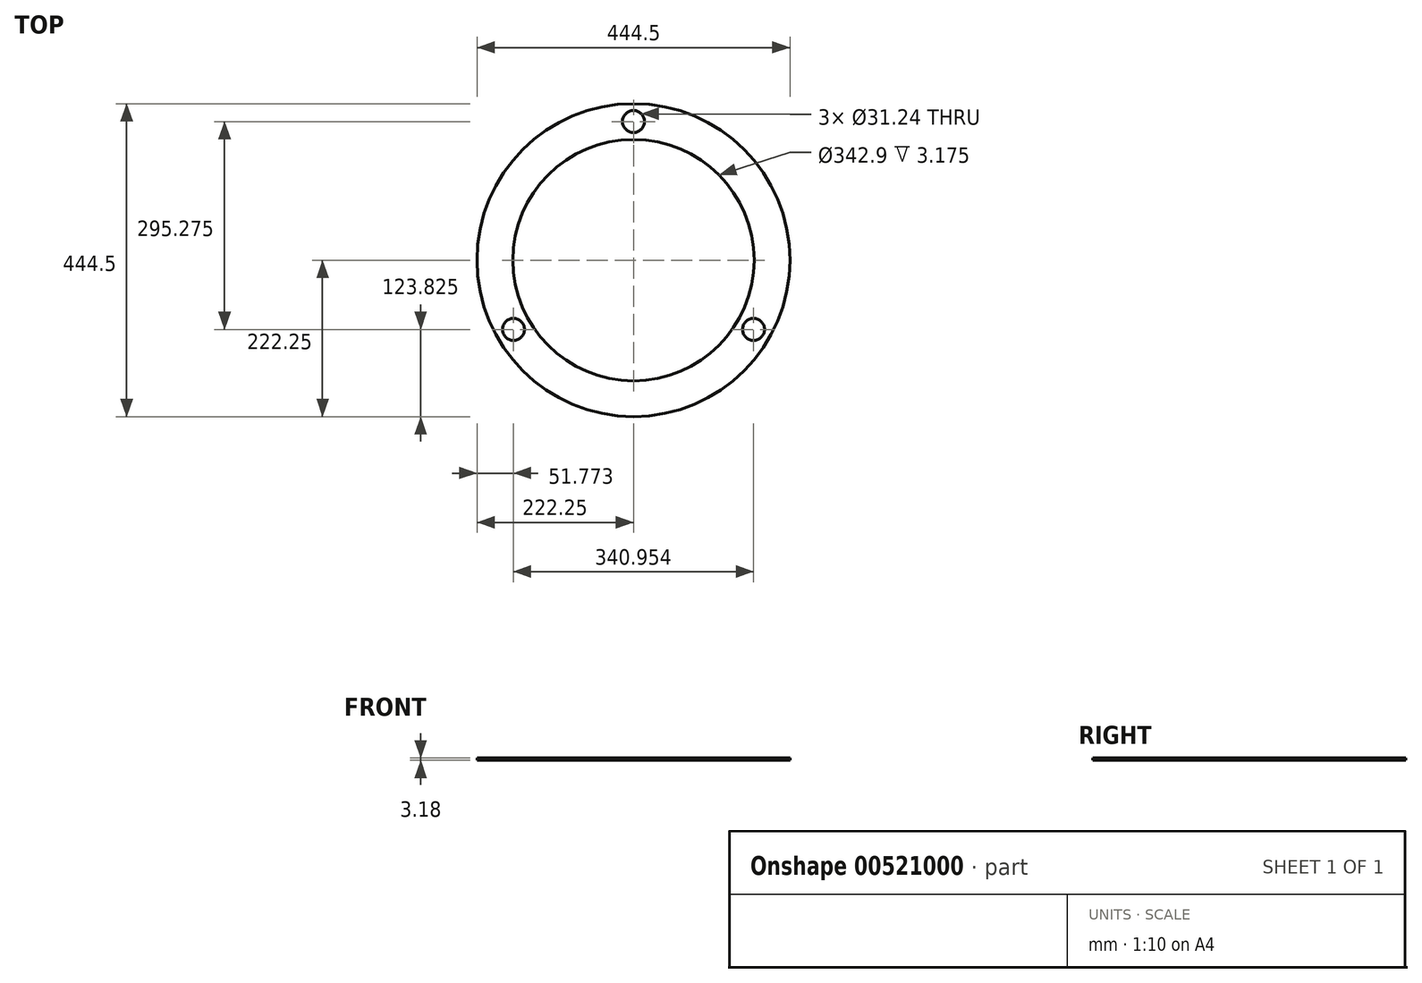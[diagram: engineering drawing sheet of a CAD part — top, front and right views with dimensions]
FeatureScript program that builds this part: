
annotation { "Feature Type Name" : "Feature", "Feature Type Description" : "" }
export const myFeature = defineFeature(function(context is Context, id is Id, definition is map)
    precondition{}
    {
        {
            var Q0;
            Q0=qCreatedBy(makeId("Top.planeOp"),FACE);
            var sketch = newSketch(context, id + "F0", { "sketchPlane" : qUnion([Q0])});
            skCircle(sketch, "E0", {"center": v(0, 0) * mm, "radius": 222.25 * mm});
            skCircle(sketch, "E1", {"center": v(0, 0) * mm, "radius": 171.45 * mm});
            skCircle(sketch, "E2", {"center": v(0, 196.85) * mm, "radius": 15.62 * mm});
            skCircle(sketch, "E3", {"center": v(170.48, -98.43) * mm, "radius": 15.62 * mm});
            skLineSegment(sketch, "E4", {"start": v(0, 259.12) * mm, "end": v(0, -278.93) * mm, "construction": true});
            skLineSegment(sketch, "E5", {"start": v(0, 0) * mm, "end": v(289.5, -167.14) * mm, "construction": true});
            skLineSegment(sketch, "E6", {"start": v(0, 0) * mm, "end": v(-307.83, -177.73) * mm, "construction": true});
            skCircle(sketch, "E7", {"center": v(-170.48, -98.43) * mm, "radius": 15.62 * mm});
            skSolve(sketch);
        }
        {
            var Q0;
            Q0=makeQuery(id+"F0.imprint","IMPRINT",FACE,{"disambiguationData":[TD([[makeQuery(id+"F0.imprint","IMPRINT",EDGE,{"derivedFrom":sQuery(id+"F0.wireOp",EDGE,"E0")}),1.0]])]});
            extrude(context, id + "F1", {"entities" : qUnion([Q0]), "endBound" : BoundingType.SYMMETRIC, "depth" : 3.17 * mm, "offsetDistance" : 25.4 * mm});
        }
    });
